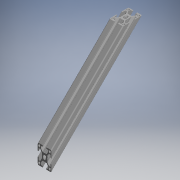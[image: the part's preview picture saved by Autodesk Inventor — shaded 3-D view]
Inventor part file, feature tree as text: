
AUTODESK INVENTOR PART (.ipt)
format: ipt  version: 2017.3 (Build 213256000, 256)  size: 304,640 bytes
history: native  units: mm (DEFAULTED — no unit token found)
features: other x14, sketch x5, extrude x3, revolve x2
ambient origin geometry x8: Origin, YZ Plane, XZ Plane, XY Plane, X Axis, Y Axis, Z Axis, Center Point
bodies: Solid1 (feature_tree)
feature tree (24):
  extrude  "Extrusion1"  Depth=400.0mm TaperAngle=0.0deg
  extrude  "Extrusion2"  TaperAngle=360.0deg  [1 undecoded]
  extrude  "Extrusion3"  TaperAngle=0.0deg  [1 undecoded]
  revolve  "Revolution1"  [1 undecoded]
  revolve  "Revolution2"  [1 undecoded]
  other  "bolt1_XY"
  other  "bolt1_YZ"
  other  "bolt1_ZX"
  other  "bolt1_X"
  other  "bolt1_Y"
  other  "bolt1_Z"
  other  "bolt1_Center"
  other  "bolt2_XY"
  other  "bolt2_YZ"
  other  "bolt2_ZX"
  other  "bolt2_X"
  other  "bolt2_Y"
  other  "bolt2_Z"
  other  "bolt2_Center"
  sketch  "Sketch_1"  dims[d0=284.842712mm d1=0.0mm d2=400.0mm d3=0.0mm]
  sketch  "Sketch_2"  dims[d4=400.0mm d5=0.0mm d6=360.0deg]
  sketch  "Sketch_3"  dims[d7=360.0deg d8=0.0mm d9=0.0mm]
  sketch  "Sketch_4"
  sketch  "Sketch_5"
note: 4 required parameter values undecoded (feature->parameter linkage not recoverable at this tier; creation-order binding heuristic only, values carry confidence <= 0.55)
